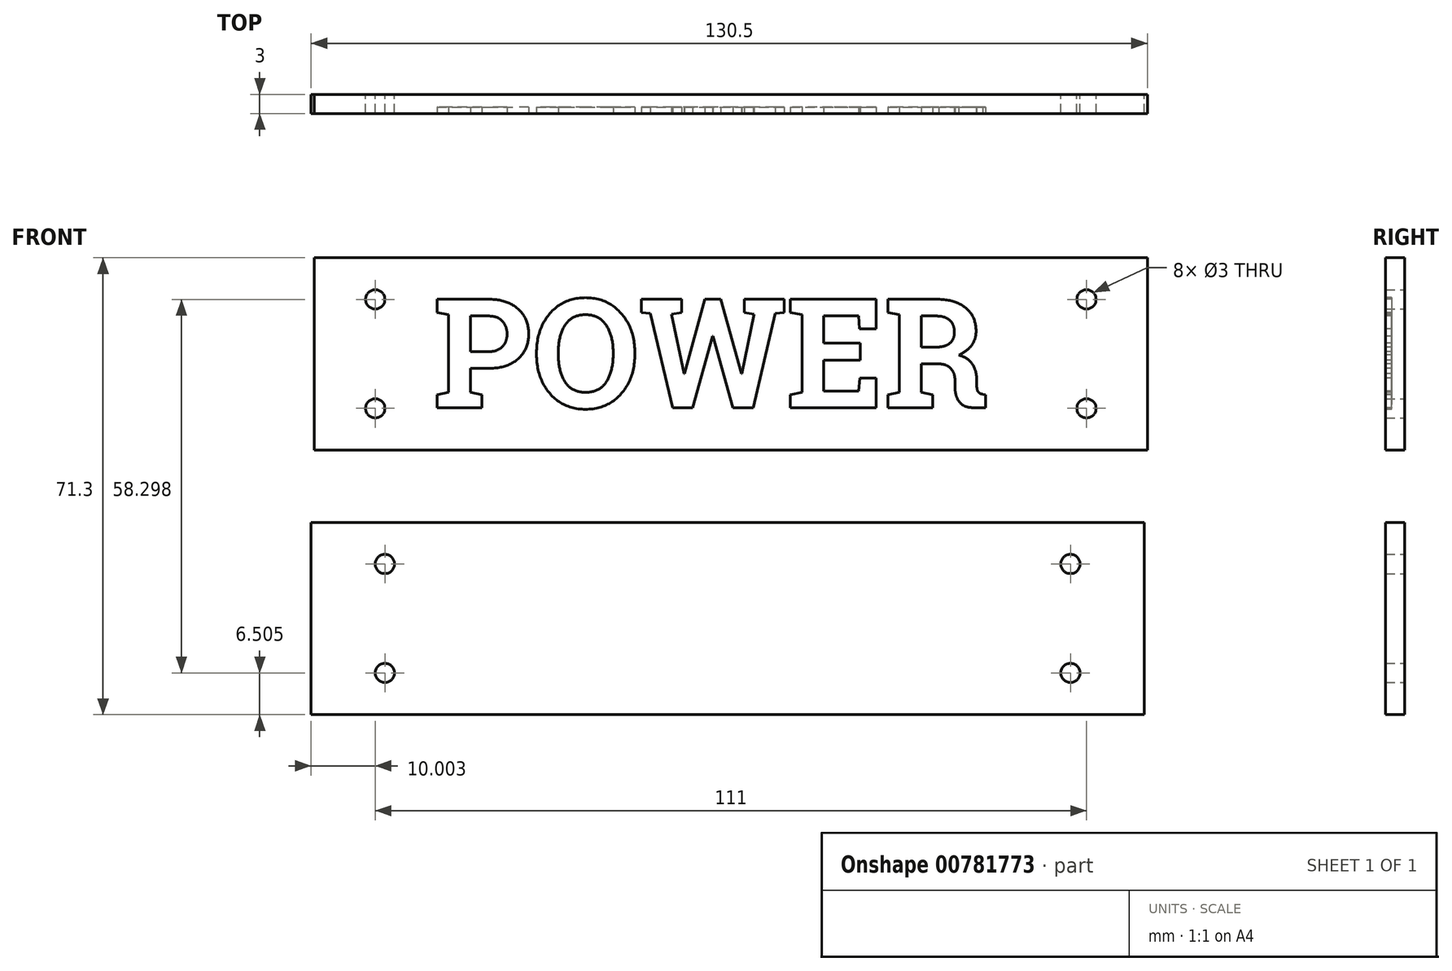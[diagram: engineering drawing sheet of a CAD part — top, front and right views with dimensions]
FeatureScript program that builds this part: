
annotation { "Feature Type Name" : "Feature", "Feature Type Description" : "" }
export const myFeature = defineFeature(function(context is Context, id is Id, definition is map)
    precondition{}
    {
        {
            var Q0;
            Q0=qCreatedBy(makeId("Front.planeOp"),FACE);
            var sketch = newSketch(context, id + "F0", { "sketchPlane" : qUnion([Q0])});
            skLineSegment(sketch, "E0.bottom", {"start": v(-61.35, 16.2) * mm, "end": v(68.65, 16.2) * mm});
            skLineSegment(sketch, "E0.top", {"start": v(-61.35, -13.8) * mm, "end": v(68.65, -13.8) * mm});
            skLineSegment(sketch, "E0.left", {"start": v(-61.35, 16.2) * mm, "end": v(-61.35, -13.8) * mm});
            skLineSegment(sketch, "E0.right", {"start": v(68.65, 16.2) * mm, "end": v(68.65, -13.8) * mm});
            skCircle(sketch, "E1", {"center": v(-51.85, 9.7) * mm, "radius": 1.5 * mm});
            skCircle(sketch, "E2", {"center": v(-51.85, -7.3) * mm, "radius": 1.5 * mm});
            skCircle(sketch, "E3", {"center": v(59.15, -7.3) * mm, "radius": 1.5 * mm});
            skCircle(sketch, "E4", {"center": v(59.15, 9.7) * mm, "radius": 1.5 * mm});
            skSolve(sketch);
        }
        {
            var Q0;
            Q0=makeQuery(id+"F0.imprint","IMPRINT",FACE,{"disambiguationData":[TD([[makeQuery(id+"F0.imprint","IMPRINT",EDGE,{"derivedFrom":sQuery(id+"F0.wireOp",EDGE,"E0.bottom")}),-1.0]])]});
            extrude(context, id + "F1", {"entities" : qUnion([Q0]), "depth" : (3) * mm, "offsetDistance" : 25 * mm});
        }
        {
            var Q0;
            Q0=makeQuery(id+"F1.opExtrude","CAP_FACE",FACE,{"disambiguationData":[OSD([sQuery(id+"F0.wireOp",EDGE,"E0.bottom"),sQuery(id+"F0.wireOp",EDGE,"E0.top"),sQuery(id+"F0.wireOp",EDGE,"E0.left"),sQuery(id+"F0.wireOp",EDGE,"E0.right"),sQuery(id+"F0.wireOp",EDGE,"E1"),sQuery(id+"F0.wireOp",EDGE,"E2"),sQuery(id+"F0.wireOp",EDGE,"E3"),sQuery(id+"F0.wireOp",EDGE,"E4")])],"isStart":false});
            var sketch = newSketch(context, id + "F2", { "sketchPlane" : qUnion([Q0])});
            skText(sketch, "E5", { "text": "POWER", "fontName": "RobotoSlab-Bold.ttf"});
            const initialGuessF2  = {"E5": [-0.04286, -0.0072, 1, 0, 0.01714]};
            skSetInitialGuess(sketch, initialGuessF2);
            skSolve(sketch);
        }
        {
            var Q0;
            Q0 = qSketchRegion(id + "F2", true);
            var Q1;
            Q1=makeQuery(id+"F1.opExtrude","CAP_FACE",FACE,{"disambiguationData":[OSD([sQuery(id+"F0.wireOp",EDGE,"E0.bottom"),sQuery(id+"F0.wireOp",EDGE,"E0.top"),sQuery(id+"F0.wireOp",EDGE,"E0.left"),sQuery(id+"F0.wireOp",EDGE,"E0.right"),sQuery(id+"F0.wireOp",EDGE,"E1"),sQuery(id+"F0.wireOp",EDGE,"E2"),sQuery(id+"F0.wireOp",EDGE,"E3"),sQuery(id+"F0.wireOp",EDGE,"E4")])],"isStart":true});
            extrude(context, id + "F3", {"entities" : qUnion([Q0, Q1]), "operationType" : NewBodyOperationType.REMOVE, "oppositeDirection" : true, "depth" : 1 * mm, "offsetDistance" : 25 * mm});
        }
        {
            var Q0;
            Q0=qCreatedBy(makeId("Front.planeOp"),FACE);
            var sketch = newSketch(context, id + "F4", { "sketchPlane" : qUnion([Q0])});
            skLineSegment(sketch, "E6.bottom", {"start": v(-61.85, -25.1) * mm, "end": v(68.15, -25.1) * mm});
            skLineSegment(sketch, "E6.top", {"start": v(-61.85, -55.1) * mm, "end": v(68.15, -55.1) * mm});
            skLineSegment(sketch, "E6.left", {"start": v(-61.85, -25.1) * mm, "end": v(-61.85, -55.1) * mm});
            skLineSegment(sketch, "E6.right", {"start": v(68.15, -25.1) * mm, "end": v(68.15, -55.1) * mm});
            skCircle(sketch, "E7", {"center": v(-50.35, -31.6) * mm, "radius": 1.5 * mm});
            skCircle(sketch, "E8", {"center": v(-50.35, -48.6) * mm, "radius": 1.5 * mm});
            skCircle(sketch, "E9", {"center": v(56.65, -48.6) * mm, "radius": 1.5 * mm});
            skCircle(sketch, "E10", {"center": v(56.65, -31.6) * mm, "radius": 1.5 * mm});
            skSolve(sketch);
        }
        {
            var Q0;
            Q0=makeQuery(id+"F4.imprint","IMPRINT",FACE,{"disambiguationData":[TD([[makeQuery(id+"F4.imprint","IMPRINT",EDGE,{"derivedFrom":sQuery(id+"F4.wireOp",EDGE,"E6.bottom")}),-1.0]])]});
            extrude(context, id + "F5", {"entities" : qUnion([Q0]), "depth" : (3) * mm, "offsetDistance" : 25 * mm});
        }
    });
